# Revit family: DBLTD_TheSenatorGroup_ChairsSeatsAndBenches_Sybr_US
name_source: partatom
category: Furniture
units: mm (PartAtom-declared; Revit-internal decimal feet)

## family parameters
Always vertical = Yes
Cut with Voids When Loaded = No
OmniClass Number = 23.40.20.00
OmniClass Title = General Furniture and Specialties
Room Calculation Point = No
Shared = Yes
Work Plane-Based = No

## types (1)
- Gaming Chair
    Assembly Code = E2020200
    AssetType = Movable
    Category = Pr_40_50_12 Chairs, seats and benches
    Color = Seat & Back: Oak Veneer or Black Colour Wash. Frame: Black or White.
    Constituents = Soft Wheel Castors / Hard Wheel Castors – both with a Solid Castor or Hollow Castor
    Cost = 0 $
    Default Elevation = 0 "
    Description = Gaming Chair
    DurationUnit = years
    ExpectedLife = 5
    Finish = Black/Grey Textile with White / Red / Yellow / or Black side trim
    Keynote = Pr_40_50_12 Chairs, seats and benches
    Manufacturer = The Senator Group
    ManufacturerName = The Senator Group
    ManufacturerURL = https://sybronline.com
    Material = Plastic Structural Seat and Back, with Moulded Foam Seat Cushion / Back Cushion / headrest, Plastic Arms with PU Armpad, Plastic / Metal Mechanism
    Model = SI1
    ModelNumber = SI1
    ModelReference = Gaming Chair
    Name = Chair
    NominalDepth = 29.25 "
    NominalHeight = 52.25 "
    NominalWidth = 29.25 "
    ProductInformation = https://sybronline.com
    SeatingBackCushionMaterial = DBLTD_TheSenatorGroup_Fabric_DarkGrey
    SeatingHeight = 17 "
    SeatingSeatCushionMaterial = DBLTD_TheSenatorGroup_Fabric_Black
    Shape = Rectangular
    Size = 29.25 x 29.25 x 52.25 "
    Type Comments = Gaming Chair
    URL = www.sybronline.com
www.sybronline.com
Gaming Chair
SI1
Gaming Chair
SI1
Gaming Chair
UK=540mm US=21.25”
UK=430mm US=17”
UK=700mm US=29.25”
UK=1330mm US=52.25”
UK=700mm US=29.25”
UK=500mm US=19.75”
https://sybronline.com
    Uniclass2015Code = Pr_40_50_12
    Uniclass2015Title = Chairs, seats and benches
    Uniclass2015Version = Products v1.15
    Version = 1
    WarrantyDescription = Senator warrants that its manufactured products are free from manufacturing defects - in materials or workmanship - for a period of ten (10) years on Senator Seating ranges; and fifteen (15) years on Senator Desking ranges
    WarrantyDurationLabor = 10
    WarrantyDurationParts = 10
    WarrantyDurationUnit = years
    WarrantyGuarantorLabor = https://www.thesenatorgroup.com
    WarrantyGuarantorParts = https://www.thesenatorgroup.com

## geometry (parser evidence)
native form markers: Sweep x2
no freeform markers — native parametric forms only
